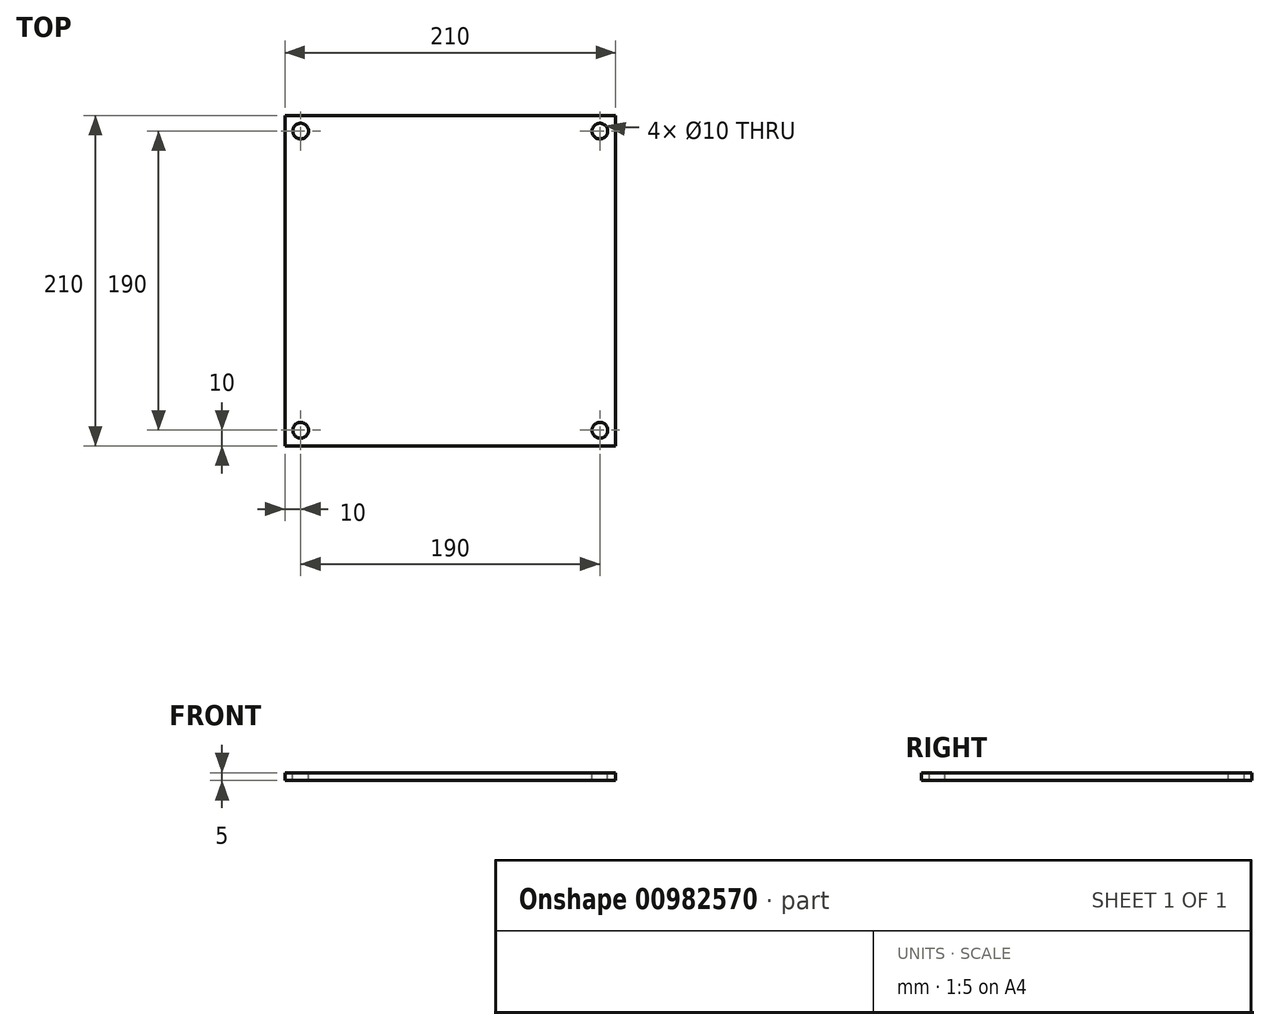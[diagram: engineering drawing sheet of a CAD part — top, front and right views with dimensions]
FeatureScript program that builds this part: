
annotation { "Feature Type Name" : "Feature", "Feature Type Description" : "" }
export const myFeature = defineFeature(function(context is Context, id is Id, definition is map)
    precondition{}
    {
        {
            var Q0;
            Q0=qCreatedBy(makeId("Top.planeOp"),FACE);
            var sketch = newSketch(context, id + "F0", { "sketchPlane" : qUnion([Q0])});
            skLineSegment(sketch, "E0.bottom", {"start": v(-105, -105) * mm, "end": v(105, -105) * mm});
            skLineSegment(sketch, "E0.top", {"start": v(-105, 105) * mm, "end": v(105, 105) * mm});
            skLineSegment(sketch, "E0.left", {"start": v(-105, -105) * mm, "end": v(-105, 105) * mm});
            skLineSegment(sketch, "E0.right", {"start": v(105, -105) * mm, "end": v(105, 105) * mm});
            skSolve(sketch);
        }
        {
            var Q0;
            Q0=qCreatedBy(makeId("Front.planeOp"),FACE);
            var sketch = newSketch(context, id + "F1", { "sketchPlane" : qUnion([Q0])});
            skLineSegment(sketch, "E1", {"start": v(0, 0) * mm, "end": v(0, 5) * mm});
            skSolve(sketch);
        }
        {
            var Q0;
            Q0=makeQuery(id+"F0.imprint","IMPRINT",FACE,{"disambiguationData":[TD([[makeQuery(id+"F0.imprint","IMPRINT",EDGE,{"derivedFrom":sQuery(id+"F0.wireOp",EDGE,"E0.bottom")}),1.0]])]});
            var Q1;
            Q1=sQuery(id+"F1.wireOp",EDGE,"E1");
            sweep(context, id + "F2", {"profiles" : qUnion([Q0]), "path" : qUnion([Q1])});
        }
        {
            var Q0;
            Q0=qCreatedBy(makeId("Top.planeOp"),FACE);
            var sketch = newSketch(context, id + "F3", { "sketchPlane" : qUnion([Q0])});
            skCircle(sketch, "E2", {"center": v(-95, -95) * mm, "radius": 5 * mm});
            skCircle(sketch, "E3", {"center": v(95, 95) * mm, "radius": 5 * mm});
            skCircle(sketch, "E4", {"center": v(-95, 95) * mm, "radius": 5 * mm});
            skCircle(sketch, "E5", {"center": v(95, -95) * mm, "radius": 5 * mm});
            skSolve(sketch);
        }
        {
            var Q0;
            Q0=qCreatedBy(makeId("Front.planeOp"),FACE);
            var sketch = newSketch(context, id + "F4", { "sketchPlane" : qUnion([Q0])});
            skLineSegment(sketch, "E6", {"start": v(0, 0) * mm, "end": v(0, 10) * mm});
            skSolve(sketch);
        }
        {
            var Q0;
            Q0 = qSketchRegion(id + "F3", true);
            var Q1;
            Q1=sQuery(id+"F4.wireOp",EDGE,"E6");
            sweep(context, id + "F5", {"operationType" : NewBodyOperationType.REMOVE, "profiles" : qUnion([Q0]), "path" : qUnion([Q1])});
        }
    });
